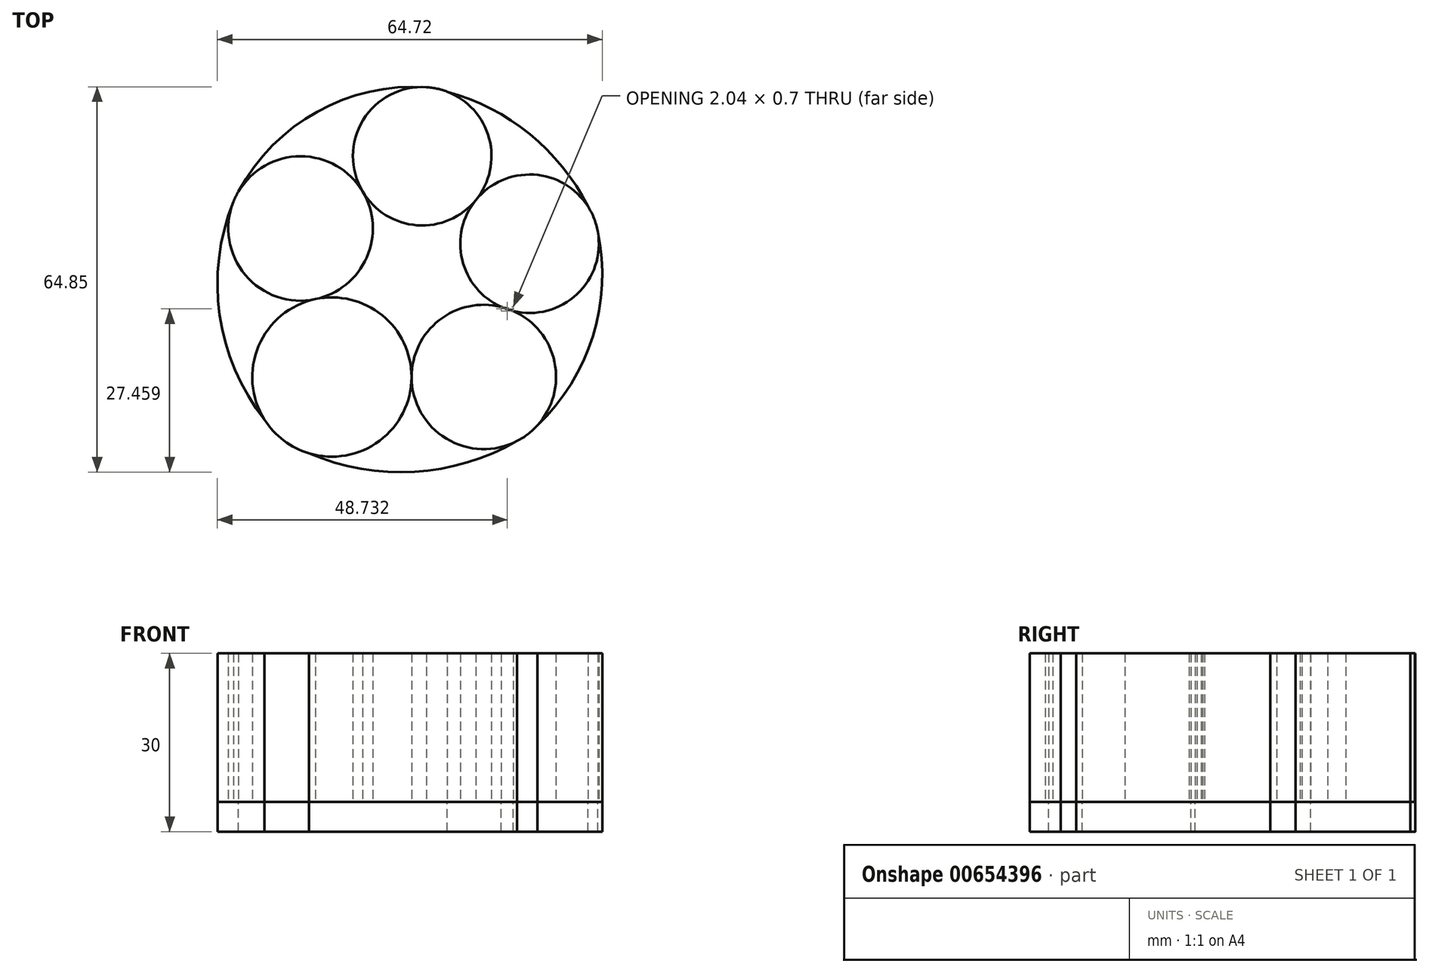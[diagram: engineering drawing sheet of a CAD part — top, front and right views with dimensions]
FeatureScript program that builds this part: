
annotation { "Feature Type Name" : "Feature", "Feature Type Description" : "" }
export const myFeature = defineFeature(function(context is Context, id is Id, definition is map)
    precondition{}
    {
        {
            var Q0;
            Q0=qCreatedBy(makeId("Top.planeOp"),FACE);
            var sketch = newSketch(context, id + "F0", { "sketchPlane" : qUnion([Q0])});
            skCircle(sketch, "E0", {"center": v(0, 0) * mm, "radius": 8.53 * mm});
            skCircle(sketch, "E1", {"center": v(0, 0) * mm, "radius": 21.93 * mm, "construction": true});
            skCircle(sketch, "E2", {"center": v(0, 0) * mm, "radius": 20.18 * mm, "construction": true});
            skCircle(sketch, "E3", {"center": v(-13.8, -17.03) * mm, "radius": 13.4 * mm});
            skCircle(sketch, "E4", {"center": v(0, 0) * mm, "radius": 20.68 * mm, "construction": true});
            skLineSegment(sketch, "E5", {"start": v(17.73, 21.87) * mm, "end": v(-22.25, -27.44) * mm, "construction": true});
            skCircle(sketch, "E6", {"center": v(-19.08, 7.97) * mm, "radius": 12.15 * mm});
            skCircle(sketch, "E7", {"center": v(11.74, -17.02) * mm, "radius": 12.15 * mm});
            skCircle(sketch, "E8", {"center": v(19.44, 5.4) * mm, "radius": 11.65 * mm});
            skCircle(sketch, "E9", {"center": v(1.38, 20.13) * mm, "radius": 11.65 * mm});
            skLineSegment(sketch, "E10", {"start": v(-5.39, -41.1) * mm, "end": v(-55.45, -0.52) * mm, "construction": true});
            skLineSegment(sketch, "E11", {"start": v(39.91, 3.88) * mm, "end": v(2, 34.62) * mm, "construction": true});
            skLineSegment(sketch, "E12", {"start": v(-2.26, -2.78) * mm, "end": v(-6.3, 0.5) * mm, "construction": true});
            skLineSegment(sketch, "E13", {"start": v(0, 0) * mm, "end": v(-30.29, 12.65) * mm, "construction": true});
            skLineSegment(sketch, "E14", {"start": v(0, 0) * mm, "end": v(2.18, 31.75) * mm, "construction": true});
            skLineSegment(sketch, "E15", {"start": v(0, 0) * mm, "end": v(30.66, 8.52) * mm, "construction": true});
            skLineSegment(sketch, "E16", {"start": v(0, 0) * mm, "end": v(18.64, -27.02) * mm, "construction": true});
            skArc(sketch, "E17", {"start": v(-30.29, 12.65) * mm, "mid": v(-32.34, -8.6) * mm, "end": v(-22.25, -27.44) * mm});
            skArc(sketch, "E18", {"start": v(2.18, 31.75) * mm, "mid": v(-17, 27.2) * mm, "end": v(-30.29, 12.65) * mm});
            skArc(sketch, "E19", {"start": v(30.66, 8.52) * mm, "mid": v(19.46, 23.86) * mm, "end": v(2.18, 31.75) * mm});
            skArc(sketch, "E20", {"start": v(18.64, -27.02) * mm, "mid": v(29.82, -11) * mm, "end": v(30.66, 8.52) * mm});
            skArc(sketch, "E21", {"start": v(-21.76, -27.82) * mm, "mid": v(-1.45, -33.02) * mm, "end": v(18.64, -27.02) * mm});
            skSolve(sketch);
        }
        {
            var Q0;
            Q0 = qSketchRegion(id + "F0", true);
            var Q1;
            {var subQ0=sQuery(id+"F0.wireOp",EDGE,"E0");var subQ4=makeQuery(id+"F0.imprint","INTERSECT",VERTEX,{"derivedFrom":[subQ0,sQuery(id+"F0.wireOp",EDGE,"E9")]});Q1=makeQuery(id+"F0.imprint","IMPRINT",FACE,{"disambiguationData":[TD([[makeQuery(id+"F0.imprint","IMPRINT",EDGE,{"disambiguationData":[TD([[subQ4,1.0]])],"derivedFrom":subQ0}),1.0]])]});}
            var Q2;
            {var subQ0=sQuery(id+"F0.wireOp",EDGE,"E6");var subQ1=sQuery(id+"F0.wireOp",EDGE,"E0");var subQ2=makeQuery(id+"F0.imprint","INTERSECT",VERTEX,{"derivedFrom":[subQ1,subQ0]});Q2=makeQuery(id+"F0.imprint","IMPRINT",FACE,{"disambiguationData":[TD([[makeQuery(id+"F0.imprint","IMPRINT",EDGE,{"disambiguationData":[TD([[subQ2,-1.0]])],"derivedFrom":subQ1}),-1.0]])]});}
            var Q3;
            {var subQ0=sQuery(id+"F0.wireOp",EDGE,"E9");var subQ1=sQuery(id+"F0.wireOp",EDGE,"E0");var subQ2=makeQuery(id+"F0.imprint","INTERSECT",VERTEX,{"derivedFrom":[subQ1,subQ0]});Q3=makeQuery(id+"F0.imprint","IMPRINT",FACE,{"disambiguationData":[TD([[makeQuery(id+"F0.imprint","IMPRINT",EDGE,{"disambiguationData":[TD([[subQ2,-1.0]])],"derivedFrom":subQ1}),-1.0]])]});}
            var Q4;
            {var subQ0=sQuery(id+"F0.wireOp",EDGE,"E9");var subQ1=sQuery(id+"F0.wireOp",EDGE,"E0");var subQ2=makeQuery(id+"F0.imprint","INTERSECT",VERTEX,{"derivedFrom":[subQ1,subQ0]});Q4=makeQuery(id+"F0.imprint","IMPRINT",FACE,{"disambiguationData":[TD([[makeQuery(id+"F0.imprint","IMPRINT",EDGE,{"disambiguationData":[TD([[subQ2,1.0]])],"derivedFrom":subQ1}),-1.0]])]});}
            var Q5;
            {var subQ0=sQuery(id+"F0.wireOp",EDGE,"E8");var subQ1=sQuery(id+"F0.wireOp",EDGE,"E0");var subQ2=makeQuery(id+"F0.imprint","INTERSECT",VERTEX,{"derivedFrom":[subQ1,subQ0]});Q5=makeQuery(id+"F0.imprint","IMPRINT",FACE,{"disambiguationData":[TD([[makeQuery(id+"F0.imprint","IMPRINT",EDGE,{"disambiguationData":[TD([[subQ2,1.0]])],"derivedFrom":subQ1}),-1.0]])]});}
            var Q6;
            {var subQ0=sQuery(id+"F0.wireOp",EDGE,"E3");var subQ1=sQuery(id+"F0.wireOp",EDGE,"E0");var subQ2=makeQuery(id+"F0.imprint","INTERSECT",VERTEX,{"derivedFrom":[subQ1,subQ0]});Q6=makeQuery(id+"F0.imprint","IMPRINT",FACE,{"disambiguationData":[TD([[makeQuery(id+"F0.imprint","IMPRINT",EDGE,{"disambiguationData":[TD([[subQ2,-1.0]])],"derivedFrom":subQ1}),-1.0]])]});}
            extrude(context, id + "F1", {"entities" : qUnion([Q0, Q1, Q2, Q3, Q4, Q5, Q6]), "oppositeDirection" : true, "depth" : 5 * mm, "offsetDistance" : 25 * mm});
        }
        {
            var Q0;
            {var subQ0=sQuery(id+"F0.wireOp",EDGE,"E17");var subQ1=sQuery(id+"F0.wireOp",EDGE,"E3");var subQ2=makeQuery(id+"F0.imprint","INTERSECT",VERTEX,{"disambiguationData":[OD(1.0)],"derivedFrom":[subQ1,subQ0]});Q0=makeQuery(id+"F0.imprint","IMPRINT",FACE,{"disambiguationData":[TD([[makeQuery(id+"F0.imprint","IMPRINT",EDGE,{"disambiguationData":[TD([[subQ2,1.0]])],"derivedFrom":subQ1}),-1.0]])]});}
            var Q1;
            {var subQ0=sQuery(id+"F0.wireOp",EDGE,"E9");var subQ1=sQuery(id+"F0.wireOp",EDGE,"E0");var subQ2=makeQuery(id+"F0.imprint","INTERSECT",VERTEX,{"derivedFrom":[subQ1,subQ0]});Q1=makeQuery(id+"F0.imprint","IMPRINT",FACE,{"disambiguationData":[TD([[makeQuery(id+"F0.imprint","IMPRINT",EDGE,{"disambiguationData":[TD([[subQ2,-1.0]])],"derivedFrom":subQ1}),-1.0]])]});}
            var Q2;
            {var subQ0=sQuery(id+"F0.wireOp",EDGE,"E9");var subQ1=sQuery(id+"F0.wireOp",EDGE,"E0");var subQ2=makeQuery(id+"F0.imprint","INTERSECT",VERTEX,{"derivedFrom":[subQ1,subQ0]});Q2=makeQuery(id+"F0.imprint","IMPRINT",FACE,{"disambiguationData":[TD([[makeQuery(id+"F0.imprint","IMPRINT",EDGE,{"disambiguationData":[TD([[subQ2,1.0]])],"derivedFrom":subQ1}),-1.0]])]});}
            var Q3;
            {var subQ0=sQuery(id+"F0.wireOp",EDGE,"E8");var subQ1=sQuery(id+"F0.wireOp",EDGE,"E0");var subQ2=makeQuery(id+"F0.imprint","INTERSECT",VERTEX,{"derivedFrom":[subQ1,subQ0]});Q3=makeQuery(id+"F0.imprint","IMPRINT",FACE,{"disambiguationData":[TD([[makeQuery(id+"F0.imprint","IMPRINT",EDGE,{"disambiguationData":[TD([[subQ2,1.0]])],"derivedFrom":subQ1}),-1.0]])]});}
            var Q4;
            {var subQ0=sQuery(id+"F0.wireOp",EDGE,"E3");var subQ1=sQuery(id+"F0.wireOp",EDGE,"E0");var subQ2=makeQuery(id+"F0.imprint","INTERSECT",VERTEX,{"derivedFrom":[subQ1,subQ0]});Q4=makeQuery(id+"F0.imprint","IMPRINT",FACE,{"disambiguationData":[TD([[makeQuery(id+"F0.imprint","IMPRINT",EDGE,{"disambiguationData":[TD([[subQ2,-1.0]])],"derivedFrom":subQ1}),-1.0]])]});}
            var Q5;
            {var subQ0=sQuery(id+"F0.wireOp",EDGE,"E21");var subQ1=sQuery(id+"F0.wireOp",EDGE,"E3");var subQ2=makeQuery(id+"F0.imprint","INTERSECT",VERTEX,{"disambiguationData":[OD(1.0)],"derivedFrom":[subQ1,subQ0]});Q5=makeQuery(id+"F0.imprint","IMPRINT",FACE,{"disambiguationData":[TD([[makeQuery(id+"F0.imprint","IMPRINT",EDGE,{"disambiguationData":[TD([[subQ2,-1.0]])],"derivedFrom":subQ1}),-1.0]])]});}
            var Q6;
            {var subQ0=sQuery(id+"F0.wireOp",EDGE,"E20");var subQ1=sQuery(id+"F0.wireOp",EDGE,"E7");var subQ2=makeQuery(id+"F0.imprint","INTERSECT",VERTEX,{"derivedFrom":[subQ1,subQ0]});Q6=makeQuery(id+"F0.imprint","IMPRINT",FACE,{"disambiguationData":[TD([[makeQuery(id+"F0.imprint","IMPRINT",EDGE,{"disambiguationData":[TD([[subQ2,-1.0]])],"derivedFrom":subQ1}),-1.0]])]});}
            var Q7;
            {var subQ0=sQuery(id+"F0.wireOp",EDGE,"E19");var subQ1=sQuery(id+"F0.wireOp",EDGE,"E8");var subQ2=makeQuery(id+"F0.imprint","INTERSECT",VERTEX,{"derivedFrom":[subQ1,subQ0]});Q7=makeQuery(id+"F0.imprint","IMPRINT",FACE,{"disambiguationData":[TD([[makeQuery(id+"F0.imprint","IMPRINT",EDGE,{"disambiguationData":[TD([[subQ2,-1.0]])],"derivedFrom":subQ1}),-1.0]])]});}
            var Q8;
            {var subQ0=sQuery(id+"F0.wireOp",EDGE,"E18");var subQ1=sQuery(id+"F0.wireOp",EDGE,"E6");var subQ2=makeQuery(id+"F0.imprint","INTERSECT",VERTEX,{"disambiguationData":[OD(1.0)],"derivedFrom":[subQ1,subQ0]});Q8=makeQuery(id+"F0.imprint","IMPRINT",FACE,{"disambiguationData":[TD([[makeQuery(id+"F0.imprint","IMPRINT",EDGE,{"disambiguationData":[TD([[subQ2,1.0]])],"derivedFrom":subQ1}),-1.0]])]});}
            var Q9;
            {var subQ0=sQuery(id+"F0.wireOp",EDGE,"E0");var subQ4=makeQuery(id+"F0.imprint","INTERSECT",VERTEX,{"derivedFrom":[subQ0,sQuery(id+"F0.wireOp",EDGE,"E9")]});Q9=makeQuery(id+"F0.imprint","IMPRINT",FACE,{"disambiguationData":[TD([[makeQuery(id+"F0.imprint","IMPRINT",EDGE,{"disambiguationData":[TD([[subQ4,1.0]])],"derivedFrom":subQ0}),1.0]])]});}
            var Q10;
            {var subQ0=sQuery(id+"F0.wireOp",EDGE,"E6");var subQ1=sQuery(id+"F0.wireOp",EDGE,"E0");var subQ2=makeQuery(id+"F0.imprint","INTERSECT",VERTEX,{"derivedFrom":[subQ1,subQ0]});Q10=makeQuery(id+"F0.imprint","IMPRINT",FACE,{"disambiguationData":[TD([[makeQuery(id+"F0.imprint","IMPRINT",EDGE,{"disambiguationData":[TD([[subQ2,-1.0]])],"derivedFrom":subQ1}),-1.0]])]});}
            extrude(context, id + "F2", {"entities" : qUnion([Q0, Q1, Q2, Q3, Q4, Q5, Q6, Q7, Q8, Q9, Q10]), "depth" : 25 * mm, "offsetDistance" : 25 * mm});
        }
    });
